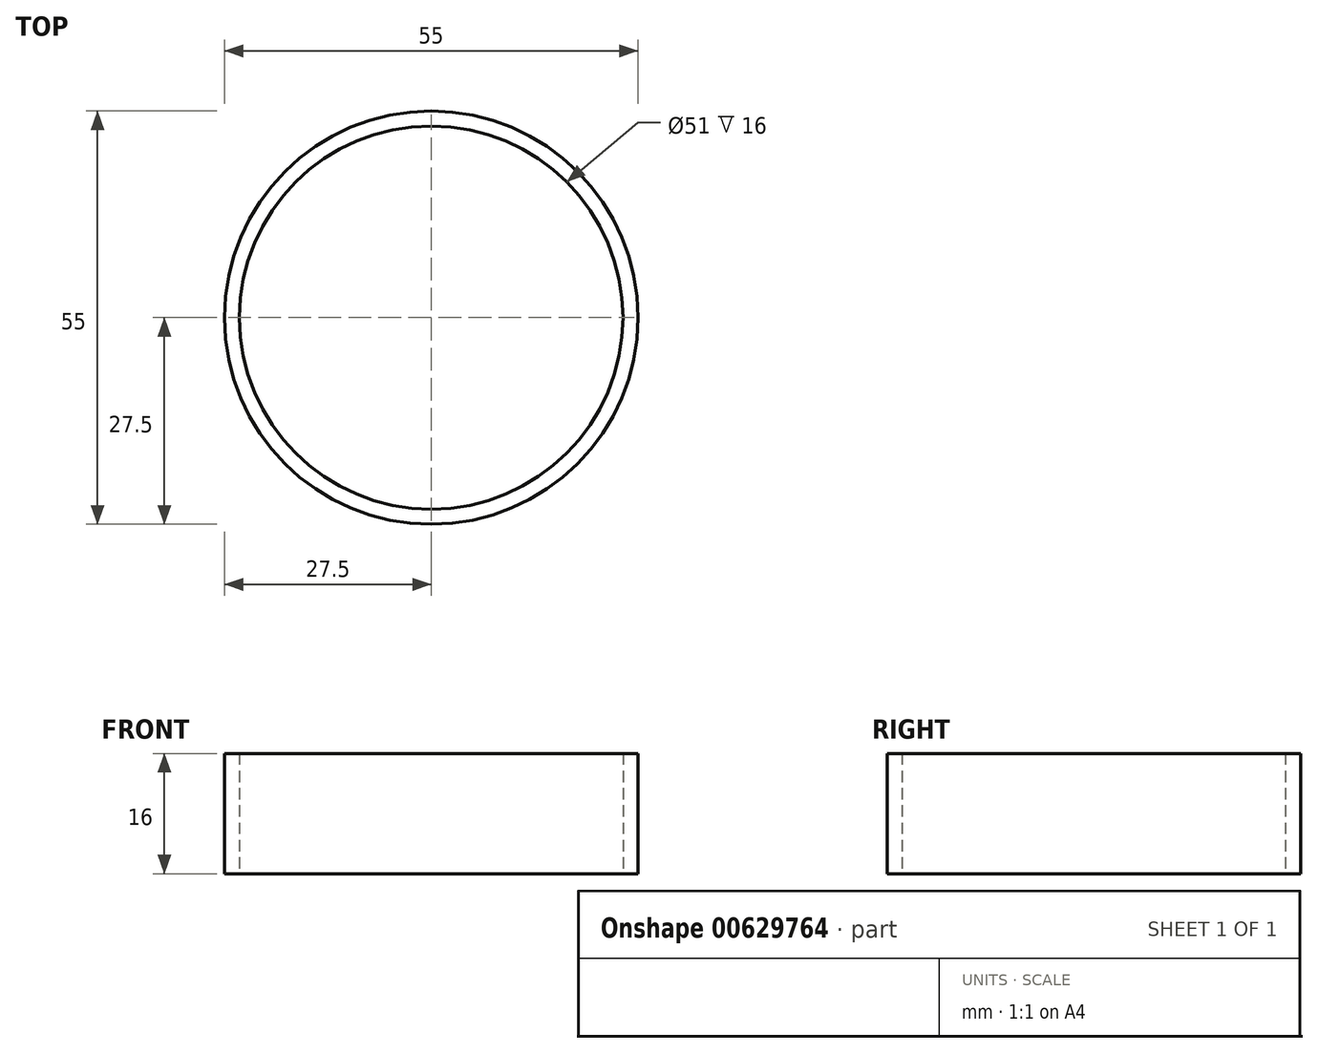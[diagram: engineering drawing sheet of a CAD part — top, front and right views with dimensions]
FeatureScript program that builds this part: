
annotation { "Feature Type Name" : "Feature", "Feature Type Description" : "" }
export const myFeature = defineFeature(function(context is Context, id is Id, definition is map)
    precondition{}
    {
        {
            var Q0;
            Q0=qCreatedBy(makeId("Top.planeOp"),FACE);
            var sketch = newSketch(context, id + "F0", { "sketchPlane" : qUnion([Q0])});
            skCircle(sketch, "E0", {"center": v(0, 0) * mm, "radius": 25.5 * mm});
            skCircle(sketch, "E1", {"center": v(0, 0) * mm, "radius": 27.5 * mm});
            skSolve(sketch);
        }
        {
            var Q0;
            Q0 = qSketchRegion(id + "F0", true);
            extrude(context, id + "F1", {"entities" : qUnion([Q0]), "depth" : 16 * mm, "offsetDistance" : 25 * mm});
        }
    });
